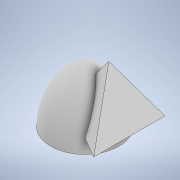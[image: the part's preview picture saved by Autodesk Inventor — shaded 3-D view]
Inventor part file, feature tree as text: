
AUTODESK INVENTOR PART (.ipt)
format: ipt  version: 2022 (Build 260153000, 153)  size: 144,384 bytes
history: native  units: mm
features: sketch x4, other x2, loft x1, revolve x1
ambient origin geometry x8: Origin, YZ Plane, XZ Plane, XY Plane, X Axis, Y Axis, Z Axis, Center Point
bodies: Body1 (feature_tree)
feature tree (8):
  other  "Твердое тело1"
  sketch  "Эскиз1"
  sketch  "Эскиз2"
  other  "РабПлоскость1"
  loft  "Лофт1"
  revolve  "Вращение1"
  sketch  "Эскиз3"
  sketch  "Эскиз7"
